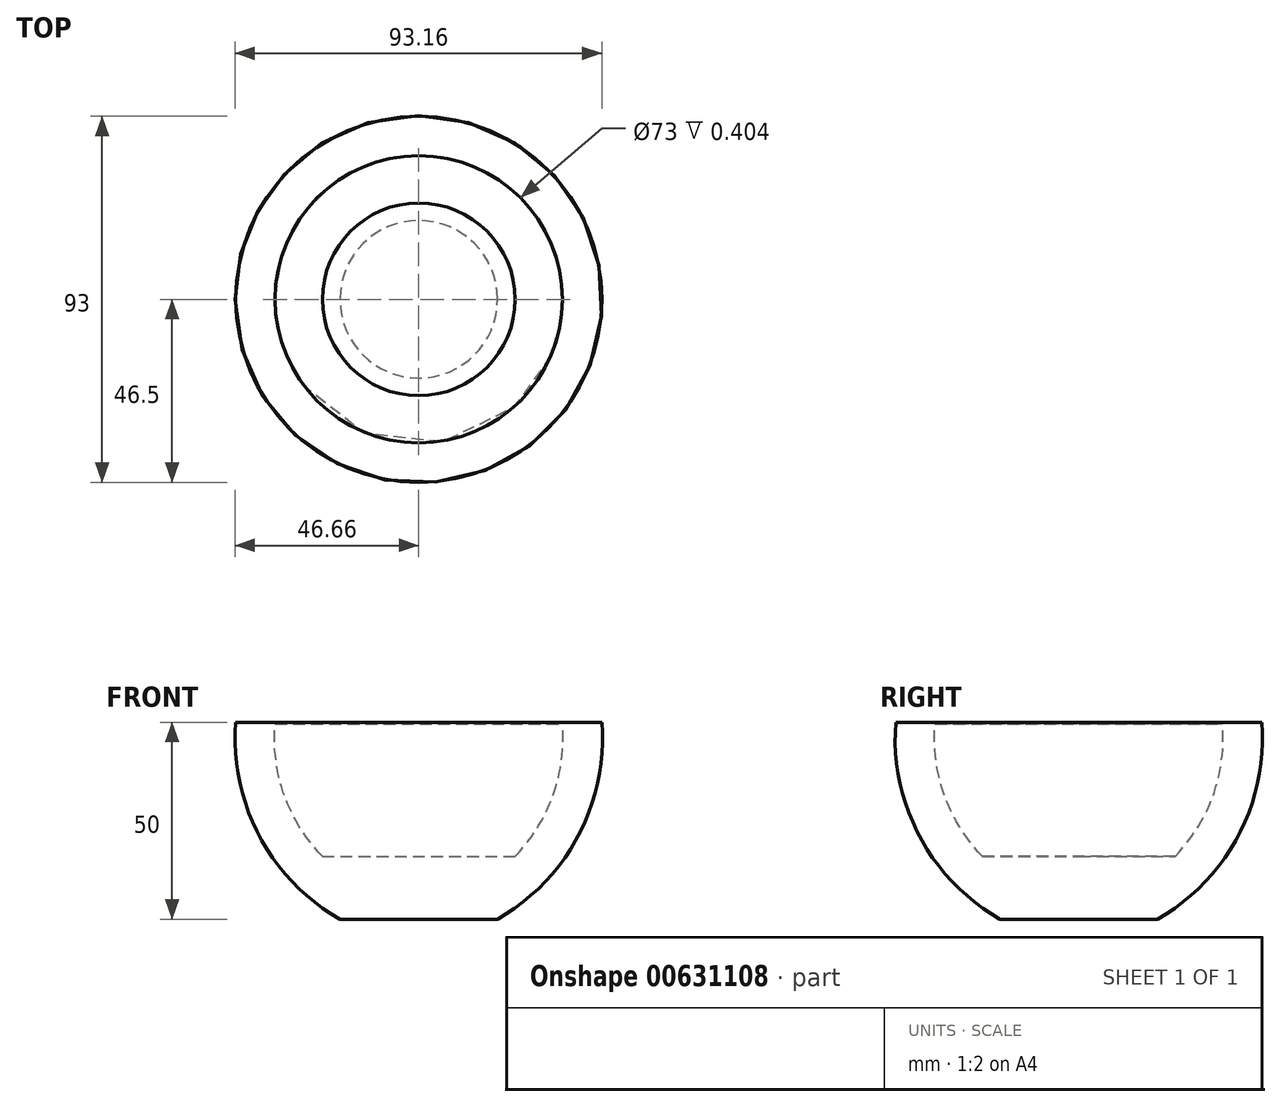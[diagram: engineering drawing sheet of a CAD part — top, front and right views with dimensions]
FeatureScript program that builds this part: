
annotation { "Feature Type Name" : "Feature", "Feature Type Description" : "" }
export const myFeature = defineFeature(function(context is Context, id is Id, definition is map)
    precondition{}
    {
        {
            var Q0;
            Q0=qCreatedBy(makeId("Front.planeOp"),FACE);
            var sketch = newSketch(context, id + "F0", { "sketchPlane" : qUnion([Q0])});
            skLineSegment(sketch, "E0", {"start": v(0, 0) * mm, "end": v(0, 16) * mm, "construction": true});
            skLineSegment(sketch, "E1", {"start": v(0, 0) * mm, "end": v(-20, 0) * mm});
            skLineSegment(sketch, "E2", {"start": v(-36.5, 50) * mm, "end": v(-46.5, 50) * mm});
            skLineSegment(sketch, "E3", {"start": v(0, 16) * mm, "end": v(0, 0) * mm});
            skArc(sketch, "E4", {"start": v(-46.5, 50) * mm, "mid": v(-40.5, 21.16) * mm, "end": v(-20, 0) * mm});
            skLineSegment(sketch, "E5", {"start": v(0, 16) * mm, "end": v(-24.48, 16) * mm});
            skLineSegment(sketch, "E6.trimOffspring", {"start": v(0, 50) * mm, "end": v(0, 80.72) * mm, "construction": true});
            skArc(sketch, "E7.0", {"start": v(-36.5, 49.6) * mm, "mid": v(-34.15, 31.5) * mm, "end": v(-24.48, 16) * mm});
            skLineSegment(sketch, "E8", {"start": v(-36.5, 50) * mm, "end": v(-36.5, 49.6) * mm});
            skSolve(sketch);
        }
        {
            var Q0;
            Q0 = qSketchRegion(id + "F0", true);
            var Q1;
            Q1=sQuery(id+"F0.wireOp",EDGE,"E0");
            revolve(context, id + "F1", {"entities" : qUnion([Q0]), "axis" : qUnion([Q1]), "revolveType" : RevolveType.FULL});
        }
    });
